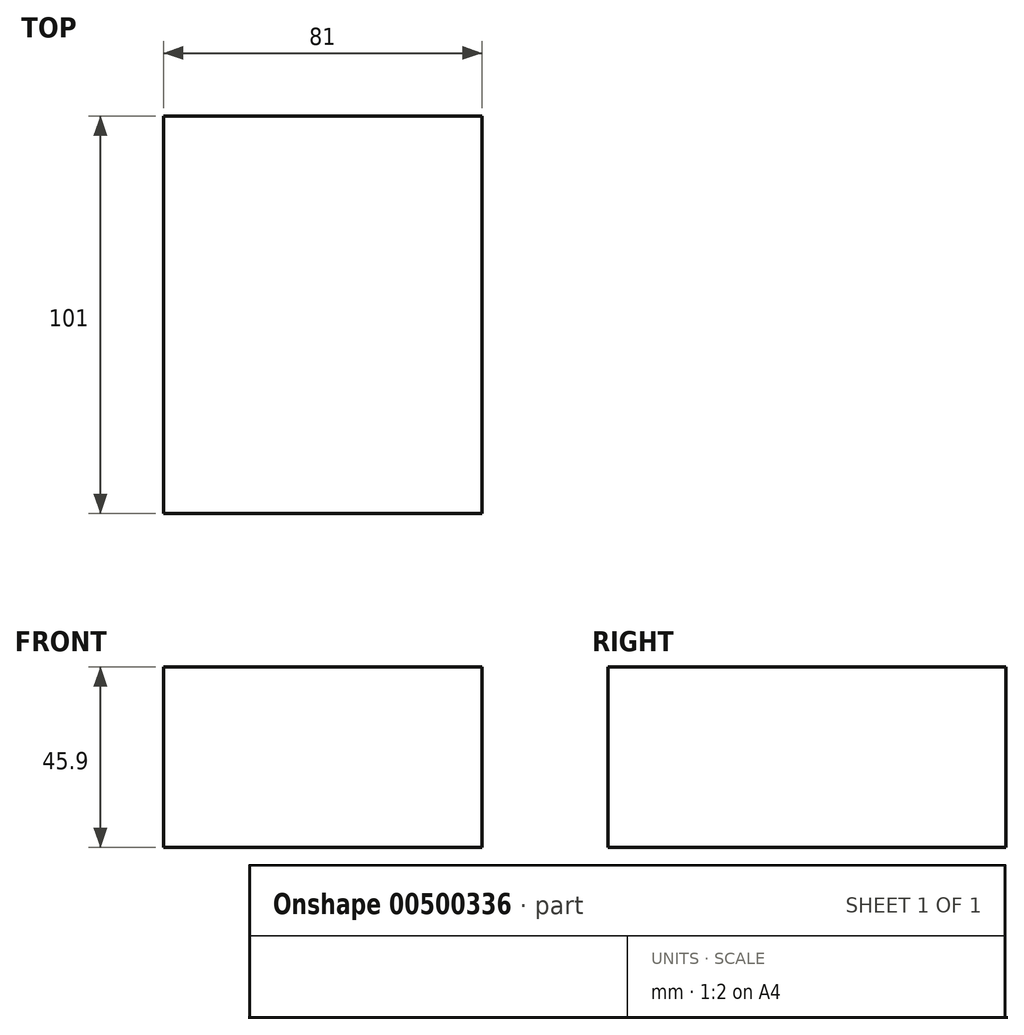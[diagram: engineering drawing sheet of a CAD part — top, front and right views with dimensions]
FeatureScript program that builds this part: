
annotation { "Feature Type Name" : "Feature", "Feature Type Description" : "" }
export const myFeature = defineFeature(function(context is Context, id is Id, definition is map)
    precondition{}
    {
        {
            var Q0;
            Q0=qCreatedBy(makeId("Front.planeOp"),FACE);
            var sketch = newSketch(context, id + "F0", { "sketchPlane" : qUnion([Q0])});
            skLineSegment(sketch, "E0.bottom", {"start": v(-40.5, -22.95) * mm, "end": v(40.5, -22.95) * mm});
            skLineSegment(sketch, "E0.top", {"start": v(-40.5, 22.95) * mm, "end": v(40.5, 22.95) * mm});
            skLineSegment(sketch, "E0.left", {"start": v(-40.5, -22.95) * mm, "end": v(-40.5, 22.95) * mm});
            skLineSegment(sketch, "E0.right", {"start": v(40.5, -22.95) * mm, "end": v(40.5, 22.95) * mm});
            skPoint(sketch, "E0.middle", {"position": v(0, 0) * mm});
            skSolve(sketch);
        }
        {
            var Q0;
            Q0 = qSketchRegion(id + "F0", true);
            extrude(context, id + "F1", {"entities" : qUnion([Q0]), "depth" : 101 * mm});
        }
    });
